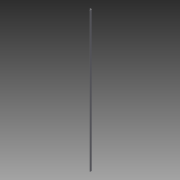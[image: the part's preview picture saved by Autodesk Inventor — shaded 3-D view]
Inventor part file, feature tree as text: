
AUTODESK INVENTOR PART (.ipt)
format: ipt  version: 2013 (Build 170138000, 138)  size: 76,800 bytes
history: native  units: in
note: dims shown in document units (in); Inventor stores cm internally (conversion verified against a paired STEP export)
features: extrude x1, sketch x1
ambient origin geometry x8: Origin, YZ Plane, XZ Plane, XY Plane, X Axis, Y Axis, Z Axis, Center Point
bodies: Solid1 (feature_tree)
feature tree (2):
  extrude  "Angle Iron Template"  Depth=1.0in
  sketch  "Sketch1"  dims[d2=0.1875in d3=1.0in d4=1.0in d5=0.1in d6=72.0in d7=0.0in]
